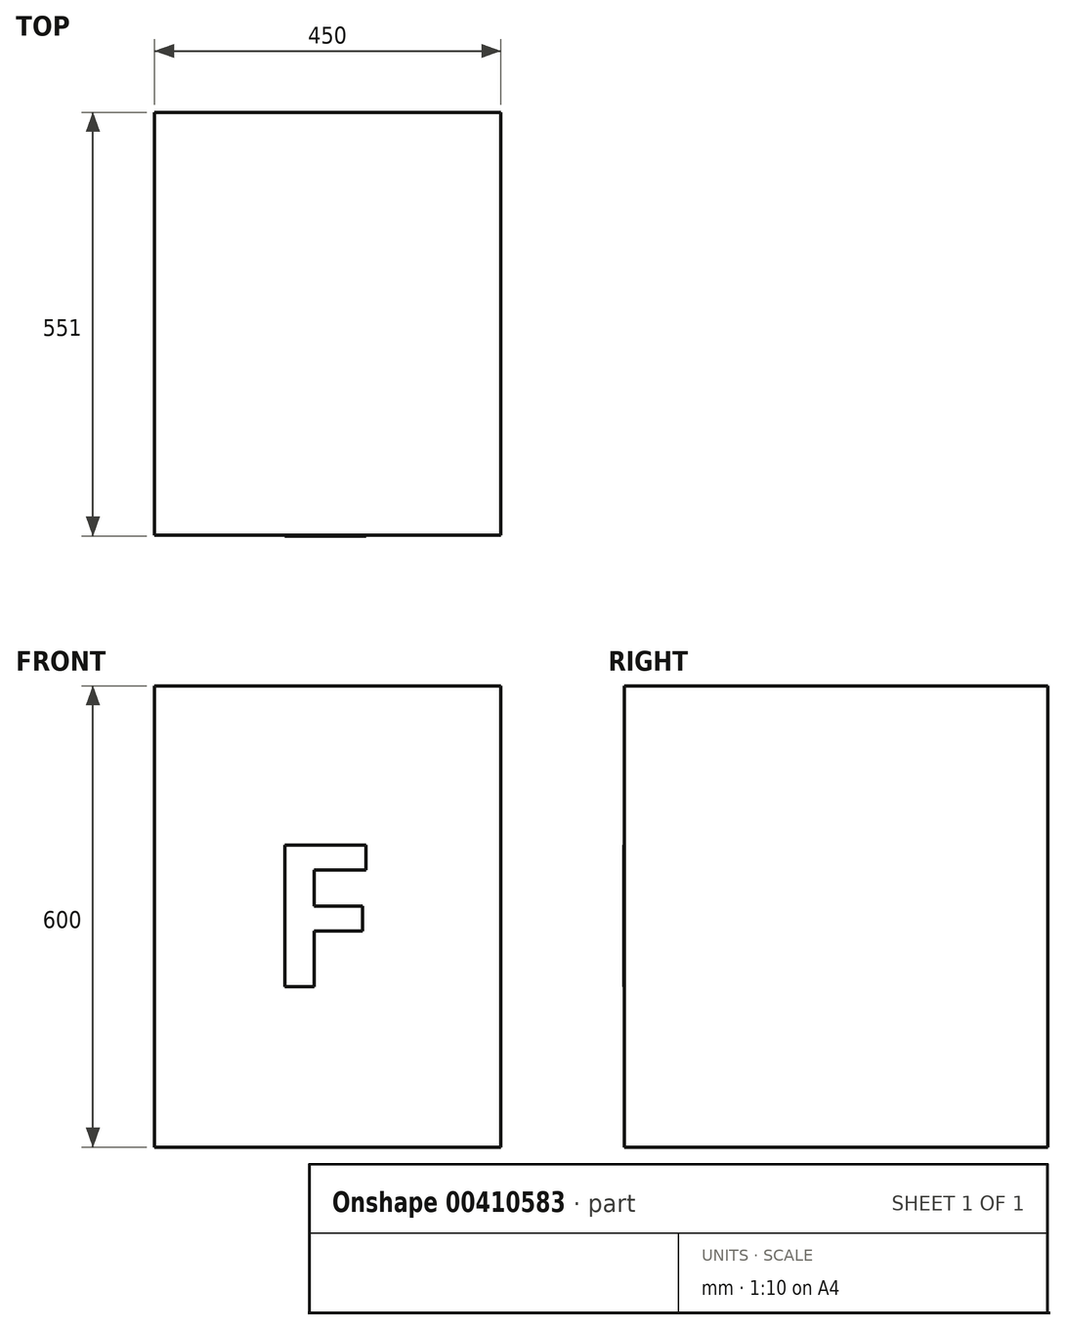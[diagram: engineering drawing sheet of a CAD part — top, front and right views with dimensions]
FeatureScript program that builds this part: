
annotation { "Feature Type Name" : "Feature", "Feature Type Description" : "" }
export const myFeature = defineFeature(function(context is Context, id is Id, definition is map)
    precondition{}
    {
        {
            var Q0;
            Q0=qCreatedBy(makeId("Top.planeOp"),FACE);
            var sketch = newSketch(context, id + "F0", { "sketchPlane" : qUnion([Q0])});
            skLineSegment(sketch, "E0.bottom", {"start": v(-225, 275) * mm, "end": v(225, 275) * mm});
            skLineSegment(sketch, "E0.top", {"start": v(-225, -275) * mm, "end": v(225, -275) * mm});
            skLineSegment(sketch, "E0.left", {"start": v(-225, 275) * mm, "end": v(-225, -275) * mm});
            skLineSegment(sketch, "E0.right", {"start": v(225, 275) * mm, "end": v(225, -275) * mm});
            skPoint(sketch, "E0.middle", {"position": v(0, 0) * mm});
            skSolve(sketch);
        }
        {
            var Q0;
            Q0=makeQuery(id+"F0.imprint","IMPRINT",FACE,{"disambiguationData":[TD([[makeQuery(id+"F0.imprint","IMPRINT",EDGE,{"derivedFrom":sQuery(id+"F0.wireOp",EDGE,"E0.bottom")}),-1.0]])]});
            extrude(context, id + "F1", {"entities" : qUnion([Q0]), "depth" : 600 * mm});
        }
        {
            var Q0;
            Q0=makeQuery(id+"F1.opExtrude","SWEPT_FACE",FACE,{"disambiguationData":[OSD([sQuery(id+"F0.wireOp",EDGE,"E0.top")])]});
            var sketch = newSketch(context, id + "F2", { "sketchPlane" : qUnion([Q0])});
            skText(sketch, "E1", { "text": "F", "fontName": "OpenSans-Bold.ttf"});
            const initialGuessF2  = {"E1": [-0.0788, 0.20853, 1, 0, 0.18563]};
            skSetInitialGuess(sketch, initialGuessF2);
            skSolve(sketch);
        }
        {
            var Q0;
            Q0=makeQuery(id+"F2.imprint","IMPRINT",FACE,{"disambiguationData":[TD([[makeQuery(id+"F2.imprint","IMPRINT",EDGE,{"derivedFrom":sQuery(id+"F2.wireOp",EDGE,"E1.sketch_text.stroke-0")}),-1.0]])]});
            extrude(context, id + "F3", {"entities" : qUnion([Q0]), "operationType" : NewBodyOperationType.ADD, "depth" : 1 * mm});
        }
    });
